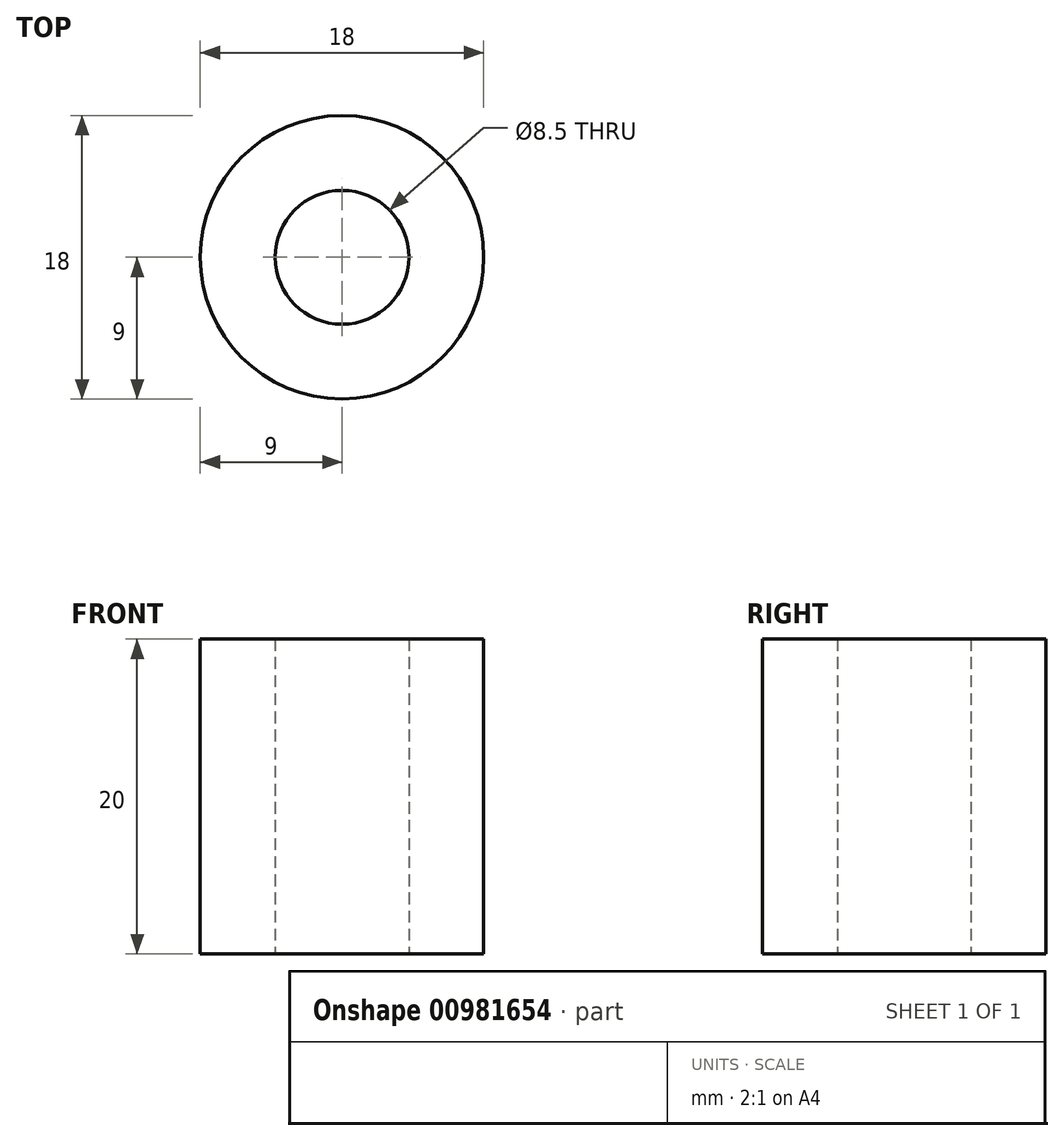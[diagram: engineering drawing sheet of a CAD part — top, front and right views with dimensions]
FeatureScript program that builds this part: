
annotation { "Feature Type Name" : "Feature", "Feature Type Description" : "" }
export const myFeature = defineFeature(function(context is Context, id is Id, definition is map)
    precondition{}
    {
        {
            var Q0;
            Q0=qCreatedBy(makeId("Top.planeOp"),FACE);
            var sketch = newSketch(context, id + "F0", { "sketchPlane" : qUnion([Q0])});
            skCircle(sketch, "E0", {"center": v(0, 0) * mm, "radius": 4.25 * mm});
            skCircle(sketch, "E1", {"center": v(0, 0) * mm, "radius": 9 * mm});
            skSolve(sketch);
        }
        {
            var Q0;
            Q0 = qSketchRegion(id + "F0", true);
            extrude(context, id + "F1", {"entities" : qUnion([Q0]), "depth" : 20 * mm, "offsetDistance" : 25 * mm});
        }
    });
